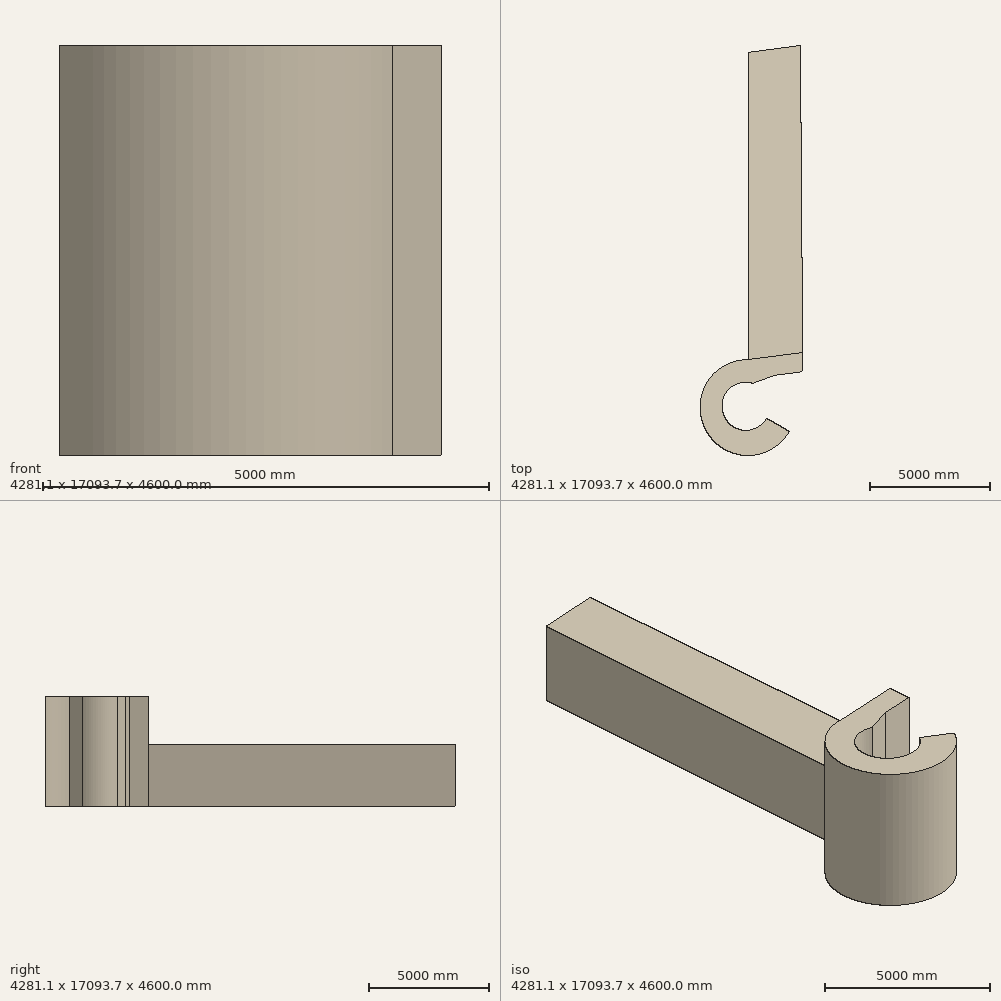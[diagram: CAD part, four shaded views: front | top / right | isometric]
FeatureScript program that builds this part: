
annotation { "Feature Type Name" : "Feature", "Feature Type Description" : "" }
export const myFeature = defineFeature(function(context is Context, id is Id, definition is map)
    precondition{}
    {
        {
            var Q0;
            Q0=qCreatedBy(makeId("Top.planeOp"),FACE);
            var sketch = newSketch(context, id + "F0", { "sketchPlane" : qUnion([Q0])});
            skLineSegment(sketch, "E0", {"start": v(0, 0) * mm, "end": v(0, -13600) * mm});
            skLineSegment(sketch, "E1", {"start": v(0, -13600) * mm, "end": v(2281.12, -13305.88) * mm});
            skLineSegment(sketch, "E2", {"start": v(2281.12, -13305.88) * mm, "end": v(2180.3, 293.74) * mm});
            skLineSegment(sketch, "E3", {"start": v(2180.3, 293.74) * mm, "end": v(0, 0) * mm});
            skSolve(sketch);
        }
        {
            var Q0;
            Q0 = qSketchRegion(id + "F0", true);
            extrude(context, id + "F1", {"entities" : qUnion([Q0]), "depth" : 2600 * mm});
        }
        {
            var Q0;
            Q0=qCreatedBy(makeId("Top.planeOp"),FACE);
            var sketch = newSketch(context, id + "F2", { "sketchPlane" : qUnion([Q0])});
            skArc(sketch, "E4", {"start": v(0, -12800) * mm, "mid": v(-1732.05, -15800) * mm, "end": v(1732.05, -15800) * mm});
            skArc(sketch, "E5", {"start": v(205, -13793.46) * mm, "mid": v(-1016.87, -15116.88) * mm, "end": v(779.42, -15250) * mm});
            skLineSegment(sketch, "E6", {"start": v(1732.05, -15800) * mm, "end": v(779.42, -15250) * mm});
            skLineSegment(sketch, "E7", {"start": v(505.81, -15723.91) * mm, "end": v(779.42, -15250) * mm, "construction": true});
            skLineSegment(sketch, "E8", {"start": v(1097, -16899.94) * mm, "end": v(1732.05, -15800) * mm, "construction": true});
            skLineSegment(sketch, "E9", {"start": v(205, -13793.46) * mm, "end": v(1140.56, -13452.94) * mm});
            skLineSegment(sketch, "E10", {"start": v(1140.56, -13452.94) * mm, "end": v(0, -13600) * mm});
            skLineSegment(sketch, "E11", {"start": v(0, -12800) * mm, "end": v(620.05, -12800) * mm, "construction": true});
            skLineSegment(sketch, "E12", {"start": v(0, -13600) * mm, "end": v(3677.3, -13600) * mm, "construction": true});
            skLineSegment(sketch, "E13", {"start": v(0, -12800) * mm, "end": v(2281.12, -12505.88) * mm});
            skLineSegment(sketch, "E14", {"start": v(2281.12, -12505.88) * mm, "end": v(2281.12, -13305.88) * mm});
            skLineSegment(sketch, "E15", {"start": v(2281.12, -13305.88) * mm, "end": v(1140.56, -13452.94) * mm});
            skSolve(sketch);
        }
        {
            var Q0;
            Q0 = qSketchRegion(id + "F2", true);
            extrude(context, id + "F3", {"entities" : qUnion([Q0]), "operationType" : NewBodyOperationType.ADD, "depth" : 4600 * mm});
        }
    });
